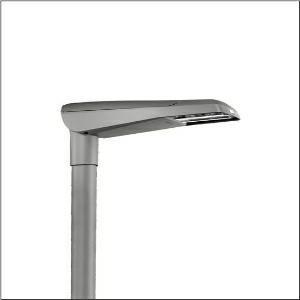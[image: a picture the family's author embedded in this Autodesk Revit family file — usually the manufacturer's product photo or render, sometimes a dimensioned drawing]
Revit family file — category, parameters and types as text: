
# Revit family: streetlight_sl_11_iq_micro___st1_0ab_5xc1n41f08ce_2768
name_source: partatom
category: Lighting Fixtures
units: mm (PartAtom-declared; Revit-internal decimal feet)

## family parameters
Cut with Voids When Loaded = No
Host = Face
Light Source = No
Part Type = Normal
Room Calculation Point = No
Round Connector Dimension = Use Diameter
Shared = No

## types (1)
- --- (1 x LED, 1650 lm, 12.6 W, 4000K)
    Apparent Load = 13 VA
    CIE Flux Codes = 29 63 95 100 100
    Color Rendering = 70
    Color Temperature = 4000K
    Default Elevation = 1800 mm
    Description = Streetlight SL 11 iQ micro, mast luminaire, primary light control with 3 zone facetted reflector, of plastic, silver coated, highly specular, primary optical cover: cover, of PMMA, transparent, light distribution: ST1.0aB, light emission: direct distribution, primary light characteristic: asymmetric, installation type: post-top, side-entry, lamps: LED, High Power LED, rated values: 1.650lm | 12,6W | 131lm/W (begin service life); end service life: 1.650lm | 12,9W; at 50% lumin. flux: 825lm | 6,8W | 121,3lm/W, colour temperature: 4000K, colour rendering: CRI > 70, light colour: 740, light setting 1 begin service life: 100% | 1.650lm | 12,6W | 131lm/W | 4.000K, light setting 1 end service life: 12,9W, further light settings possible, control: optimised constant luminous flux control (CLO 2.0), Desk-Remote (wireless, voltage-free reading and setting of iQ features in the workshop via application-optimized NFC function/RFID function), Light-Fading, Smart-Wire, Night-Set, Lumen-Switch, Temp-Guard, Auto-Match, Street-Remote, with cable H07RN-F 5x 1.5mm², mains connection: 230..240V, AC, 50/60Hz, connection cable pre-assembled, cable length: 5,5m, luminaire housing, of diecast aluminium, powder-coated, Siteco® metallic grey (DB 702S), please order mast flange separately, inclination adjustable without tools: 0°, 5°, 10°, 15° (post-top) | 0°, -5°, -10°, -15° (side-entry), sealing non-destructively replaceable, multi-level sealing system, length: 600mm, width: 174mm, height: 116mm, mast flange for spigot size: 42mm (side-entry): 5XC10008XM4, 60/48mm (side-entry/post-top): 5XC10108XM2, 76/60mm (side-entry/post-top): 5XC10108XM1, equipment: standard, protection rating (complete): IP66, insulation class (complete): insulation class II (safety insulation), certification: CE, ENEC, ENEC+, VDE, impact resistance: IK10, permissible operating ambient temperature for outdoor applications: -25..+50°C, standard-compliant lighting for roads and squares, Environmental Product Declaration (EPD) tested and certified by an independent institute, packaging unit: 1 piece

Light Distribution: ST1.0aB
    Height = 116 mm
    Lamp = 1 x LED
    Lamp Light Flux = 1650 lm
    Lamp Power = 12.6 W
    Lamp count = 1
    Length = 600 mm
    Luminous efficacy = 131 lm/W
    Manufacturer = Siteco
    ModVariant = No
    Model = 5XC1N41F08CE
    Number of Poles = 1
    OnlyDefault = Yes
    Power Factor = 1
    Product Name = Streetlight SL 11 iQ micro | ST1.0aB
    Product group = mast luminaire | pylon top
    ProductGroupID = 6100
    Protection Class = Protection class II
    Protection Degree = IP 66
    RLX_Detail_Level = 1
    RLX_Emergency_Light_Flux = 0 lm
    RLX_Emergency_Type = 0
    RLX_Emergency_Type_DB = No
    RlxData = <blob elided: 26281 chars, md5=0585d74c>
    Socket = socket
    Standby Power = 0 W
    System Light Flux = 1650 lm
    System Power = 13 W
    Type Comments = factory setting: luminous flux: 100 % | dim-lin: 254 | 229 mA
    Type Image = l_1006566.jpg
    URL = http://relux.com
    VarID = @adj_019831
    Voltage = 0 V
    Weight = 0.00 kg
    Width = 174 mm

## geometry (parser evidence)
native form markers: Blend x4, Sweep x10
no freeform markers — native parametric forms only
